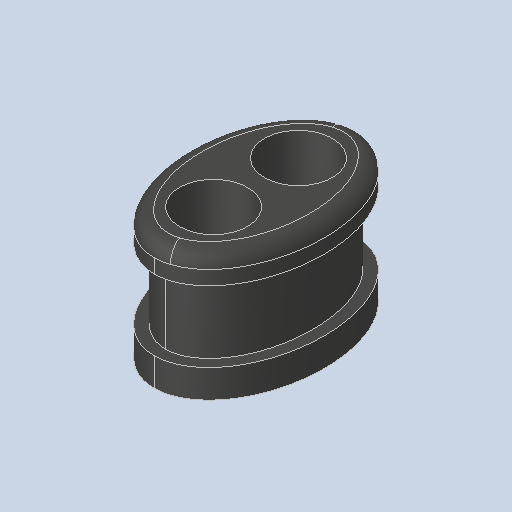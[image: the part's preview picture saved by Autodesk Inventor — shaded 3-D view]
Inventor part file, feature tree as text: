
AUTODESK INVENTOR PART (.ipt)
format: ipt  version: 2023.4 (Build 274418000, 418)  size: 172,544 bytes
history: native  units: in
note: dims shown in document units (in); Inventor stores cm internally (conversion verified against a paired STEP export)
features: fillet x1
ambient origin geometry x8: Origin, YZ Plane, XZ Plane, XY Plane, X Axis, Y Axis, Z Axis, Center Point
bodies: Solid1 (feature_tree)
feature tree (1):
  fillet  "Fillet1"  [1 undecoded]
note: 1 required parameter value undecoded (feature->parameter linkage not recoverable at this tier; creation-order binding heuristic only, values carry confidence <= 0.55)
